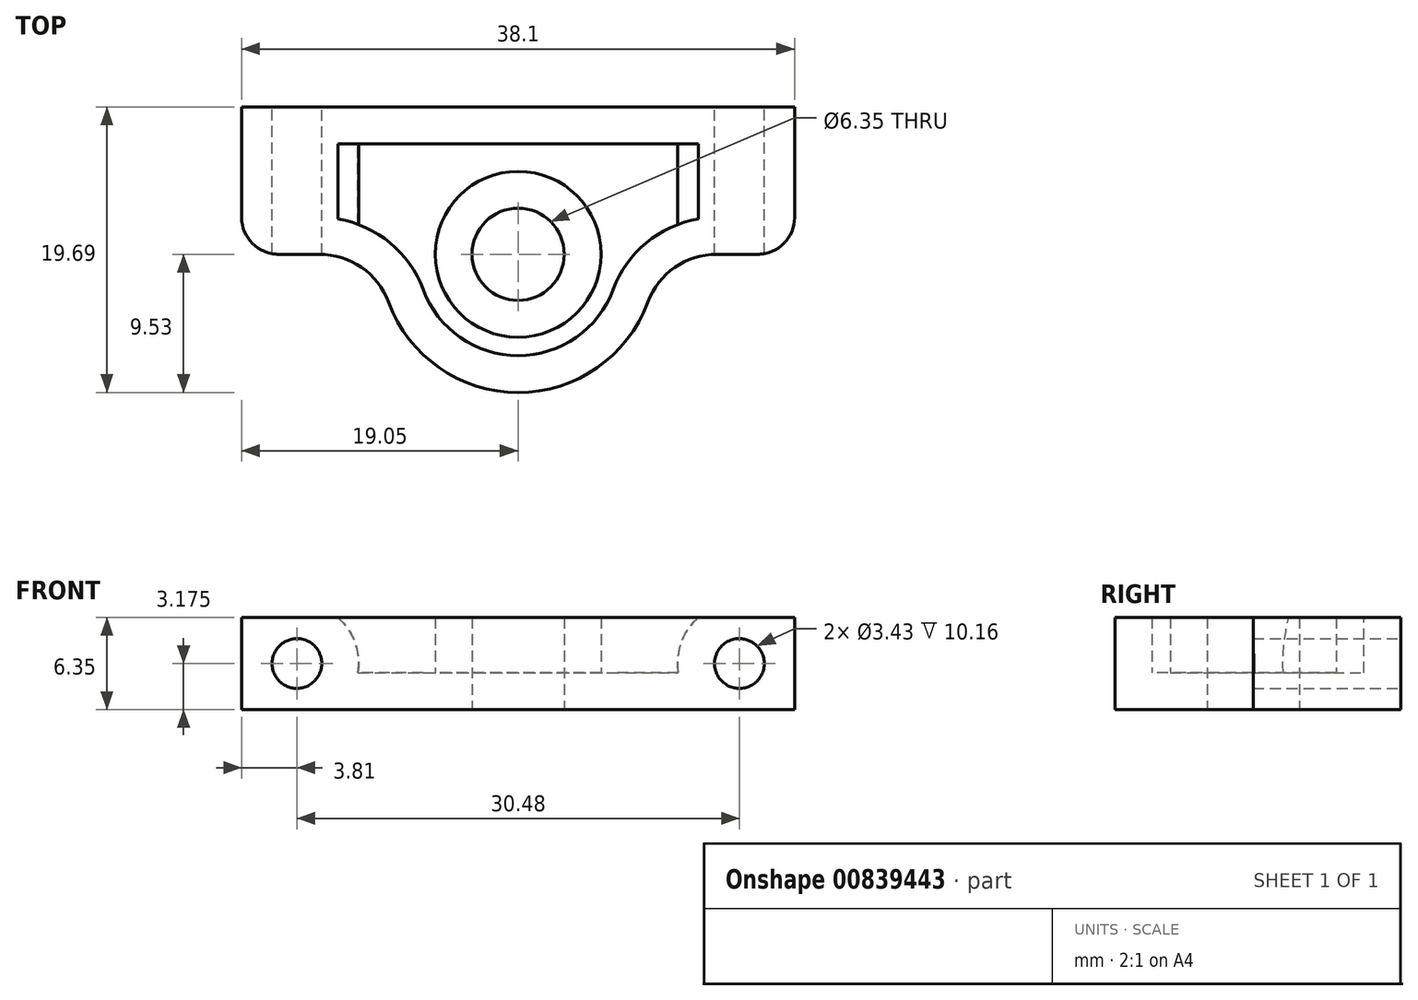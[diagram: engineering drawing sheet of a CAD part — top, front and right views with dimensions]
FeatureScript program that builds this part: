
annotation { "Feature Type Name" : "Feature", "Feature Type Description" : "" }
export const myFeature = defineFeature(function(context is Context, id is Id, definition is map)
    precondition{}
    {
        {
            var Q0;
            Q0=qCreatedBy(makeId("Top.planeOp"),FACE);
            var sketch = newSketch(context, id + "F0", { "sketchPlane" : qUnion([Q0])});
            skCircle(sketch, "E0", {"center": v(0, 0) * mm, "radius": 3.18 * mm});
            skLineSegment(sketch, "E1", {"start": v(0, 0) * mm, "end": v(0, 25.4) * mm, "construction": true});
            skLineSegment(sketch, "E2", {"start": v(0, 0) * mm, "end": v(0, -25.4) * mm, "construction": true});
            skCircle(sketch, "E3", {"center": v(0, 0) * mm, "radius": 9.53 * mm});
            skLineSegment(sketch, "E4", {"start": v(0, 0) * mm, "end": v(-19.05, 0) * mm, "construction": true});
            skLineSegment(sketch, "E5.bottom", {"start": v(-19.05, 0) * mm, "end": v(19.05, 0) * mm});
            skLineSegment(sketch, "E5.top", {"start": v(-19.05, 10.16) * mm, "end": v(19.05, 10.16) * mm});
            skLineSegment(sketch, "E5.left", {"start": v(-19.05, 0) * mm, "end": v(-19.05, 10.16) * mm});
            skLineSegment(sketch, "E5.right", {"start": v(19.05, 0) * mm, "end": v(19.05, 10.16) * mm});
            skSolve(sketch);
        }
        {
            var Q0;
            Q0 = qSketchRegion(id + "F0", true);
            extrude(context, id + "F1", {"entities" : qUnion([Q0]), "depth" : 6.35 * mm, "offsetDistance" : 25.4 * mm});
        }
        {
            var Q0;
            {var subQ0=sQuery(id+"F0.wireOp",EDGE,"E3");var subQ1=sQuery(id+"F0.wireOp",EDGE,"Xk2k9R8C-tr57-Uwgu-dlkQ-hizivi9LOOm5.top");Q0=makeQuery(id+"F1.opExtrude","SWEPT_EDGE",EDGE,{"disambiguationData":[OSD([subQ1,subQ0]),TDD([makeQuery(id+"F0.imprint","INTERSECT",VERTEX,{"disambiguationData":[OD(0.0)],"derivedFrom":[subQ1,subQ0]})])]});}
            var Q1;
            {var subQ0=sQuery(id+"F0.wireOp",EDGE,"E3");var subQ1=sQuery(id+"F0.wireOp",EDGE,"Xk2k9R8C-tr57-Uwgu-dlkQ-hizivi9LOOm5.top");Q1=makeQuery(id+"F1.opExtrude","SWEPT_EDGE",EDGE,{"disambiguationData":[OSD([subQ1,subQ0]),TDD([makeQuery(id+"F0.imprint","INTERSECT",VERTEX,{"disambiguationData":[OD(1.0)],"derivedFrom":[subQ1,subQ0]})])]});}
            var Q2;
            Q2=makeQuery(id+"F1.opExtrude","SWEPT_EDGE",EDGE,{"disambiguationData":[OSD([sQuery(id+"F0.wireOp",EDGE,"Xk2k9R8C-tr57-Uwgu-dlkQ-hizivi9LOOm5.top"),sQuery(id+"F0.wireOp",EDGE,"Xk2k9R8C-tr57-Uwgu-dlkQ-hizivi9LOOm5.right")])]});
            var Q3;
            Q3=makeQuery(id+"F1.opExtrude","SWEPT_EDGE",EDGE,{"disambiguationData":[OSD([sQuery(id+"F0.wireOp",EDGE,"Xk2k9R8C-tr57-Uwgu-dlkQ-hizivi9LOOm5.top"),sQuery(id+"F0.wireOp",EDGE,"Xk2k9R8C-tr57-Uwgu-dlkQ-hizivi9LOOm5.left")])]});
            fillet(context, id + "F2", {"entities" : qUnion([Q0, Q1, Q2, Q3]), "tangentPropagation" : true, "radius" : 5.08 * mm, "defaultsChanged" : false, "vertexSettings" : [], "allowEdgeOverflow" : false});
        }
        {
            var Q0;
            Q0=makeQuery(id+"F1.opExtrude","SWEPT_FACE",FACE,{"disambiguationData":[OSD([sQuery(id+"F0.wireOp",EDGE,"E5.top")])]});
            var sketch = newSketch(context, id + "F3", { "sketchPlane" : qUnion([Q0])});
            skCircle(sketch, "E6", {"center": v(15.24, 3.18) * mm, "radius": 1.71 * mm});
            skPoint(sketch, "E6.centerSnap0", {"position": v(19.05, 3.18) * mm});
            skCircle(sketch, "E7", {"center": v(-15.24, 3.18) * mm, "radius": 1.71 * mm});
            skSolve(sketch);
        }
        {
            var Q0;
            Q0=qCreatedBy(makeId("Front.planeOp"),FACE);
            cPlane(context, id + "F4", {"entities" : qUnion([Q0]), "cplaneType" : CPlaneType.OFFSET, "offset" : 12.7 * mm, "width" : 152.4 * mm, "height" : 152.4 * mm});
        }
        {
            var Q0;
            Q0 = qSketchRegion(id + "F3", true);
            extrude(context, id + "F5", {"entities" : qUnion([Q0]), "operationType" : NewBodyOperationType.REMOVE, "endBound" : BoundingType.THROUGH_ALL, "oppositeDirection" : true, "depth" : 25.4 * mm, "offsetDistance" : 25.4 * mm});
        }
        {
            var Q0;
            Q0=makeQuery(id+"F1.opExtrude","CAP_FACE",FACE,{"disambiguationData":[OSD([sQuery(id+"F0.wireOp",EDGE,"E0"),sQuery(id+"F0.wireOp",EDGE,"E3"),sQuery(id+"F0.wireOp",EDGE,"E5.bottom"),sQuery(id+"F0.wireOp",EDGE,"E5.top"),sQuery(id+"F0.wireOp",EDGE,"E5.left"),sQuery(id+"F0.wireOp",EDGE,"E5.right")])],"isStart":false});
            shell(context, id + "F6", {"entities" : qUnion([Q0]), "thickness" : 2.54 * mm});
        }
        {
            var Q0;
            Q0=makeQuery(id+"F1.opExtrude","SWEPT_EDGE",EDGE,{"disambiguationData":[OSD([sQuery(id+"F0.wireOp",EDGE,"E5.bottom"),sQuery(id+"F0.wireOp",EDGE,"E5.left")])]});
            var Q1;
            Q1=makeQuery(id+"F1.opExtrude","SWEPT_EDGE",EDGE,{"disambiguationData":[OSD([sQuery(id+"F0.wireOp",EDGE,"E5.bottom"),sQuery(id+"F0.wireOp",EDGE,"E5.right")])]});
            fillet(context, id + "F7", {"entities" : qUnion([Q0, Q1]), "tangentPropagation" : true, "radius" : 2.54 * mm, "defaultsChanged" : true, "vertexSettings" : [], "allowEdgeOverflow" : false});
        }
    });
